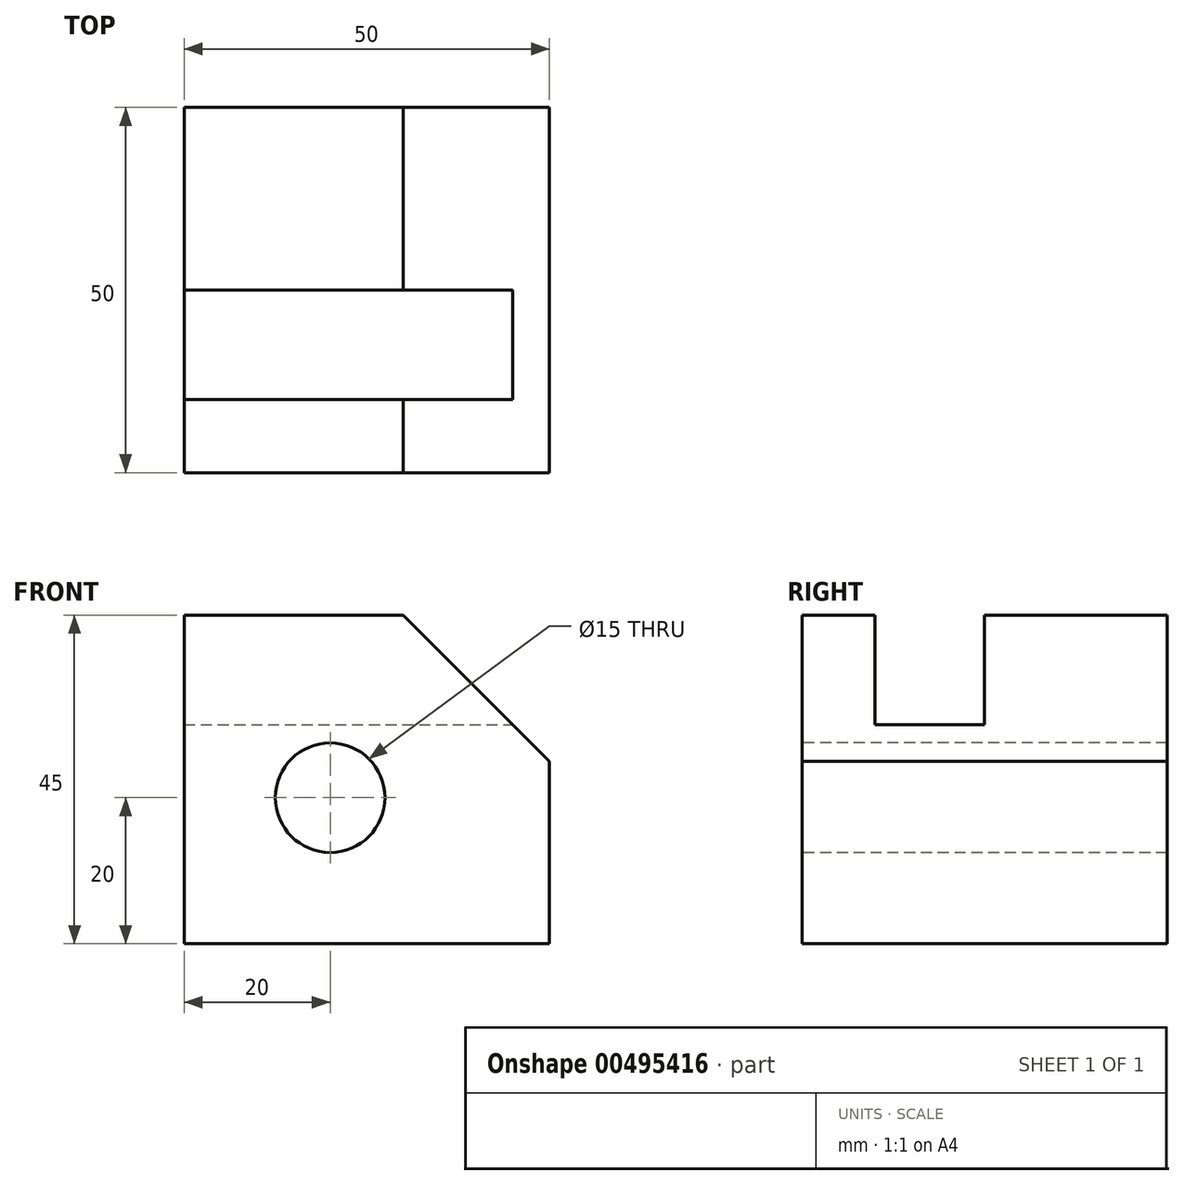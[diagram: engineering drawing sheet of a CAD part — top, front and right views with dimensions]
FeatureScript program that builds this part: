
annotation { "Feature Type Name" : "Feature", "Feature Type Description" : "" }
export const myFeature = defineFeature(function(context is Context, id is Id, definition is map)
    precondition{}
    {
        {
            var Q0;
            Q0=qCreatedBy(makeId("Front.planeOp"),FACE);
            var sketch = newSketch(context, id + "F0", { "sketchPlane" : qUnion([Q0])});
            skLineSegment(sketch, "E0", {"start": v(0, 0) * mm, "end": v(0, 45) * mm});
            skLineSegment(sketch, "E1", {"start": v(0, 45) * mm, "end": v(30, 45) * mm});
            skLineSegment(sketch, "E2", {"start": v(30, 45) * mm, "end": v(50, 25) * mm});
            skLineSegment(sketch, "E3", {"start": v(50, 25) * mm, "end": v(50, 0) * mm});
            skLineSegment(sketch, "E4", {"start": v(50, 0) * mm, "end": v(0, 0) * mm});
            skSolve(sketch);
        }
        {
            var Q0;
            Q0 = qSketchRegion(id + "F0", true);
            extrude(context, id + "F1", {"entities" : qUnion([Q0]), "depth" : 50 * mm});
        }
        {
            var Q0;
            Q0=makeQuery(id+"F1.opExtrude","CAP_FACE",FACE,{"disambiguationData":[OSD([sQuery(id+"F0.wireOp",EDGE,"E0"),sQuery(id+"F0.wireOp",EDGE,"E1"),sQuery(id+"F0.wireOp",EDGE,"E2"),sQuery(id+"F0.wireOp",EDGE,"E3"),sQuery(id+"F0.wireOp",EDGE,"E4")])],"isStart":false});
            var sketch = newSketch(context, id + "F2", { "sketchPlane" : qUnion([Q0])});
            skCircle(sketch, "E5", {"center": v(20, 20) * mm, "radius": 7.5 * mm});
            skSolve(sketch);
        }
        {
            var Q0;
            Q0 = qSketchRegion(id + "F2", true);
            extrude(context, id + "F3", {"entities" : qUnion([Q0]), "operationType" : NewBodyOperationType.REMOVE, "endBound" : BoundingType.THROUGH_ALL, "oppositeDirection" : true, "depth" : 25 * mm});
        }
        {
            var Q0;
            Q0=makeQuery(id+"F1.opExtrude","SWEPT_FACE",FACE,{"disambiguationData":[OSD([sQuery(id+"F0.wireOp",EDGE,"E4")])]});
            cPlane(context, id + "F4", {"entities" : qUnion([Q0]), "cplaneType" : CPlaneType.OFFSET, "offset" : 30 * mm, "oppositeDirection" : true, "width" : 150 * mm, "height" : 150 * mm});
        }
        {
            var Q0;
            Q0=makeQuery(id+"F1.opExtrude","SWEPT_FACE",FACE,{"disambiguationData":[OSD([sQuery(id+"F0.wireOp",EDGE,"E1")])]});
            var sketch = newSketch(context, id + "F5", { "sketchPlane" : qUnion([Q0])});
            skLineSegment(sketch, "E6.bottom", {"start": v(0, -40) * mm, "end": v(50, -40) * mm});
            skLineSegment(sketch, "E6.top", {"start": v(0, -25) * mm, "end": v(50, -25) * mm});
            skLineSegment(sketch, "E6.left", {"start": v(0, -40) * mm, "end": v(0, -25) * mm});
            skLineSegment(sketch, "E6.right", {"start": v(50, -40) * mm, "end": v(50, -25) * mm});
            skSolve(sketch);
        }
        {
            var Q0;
            Q0 = qSketchRegion(id + "F5", true);
            var Q1;
            Q1=qCreatedBy(id+"F4.planeOp",FACE);
            extrude(context, id + "F6", {"entities" : qUnion([Q0]), "operationType" : NewBodyOperationType.REMOVE, "endBound" : BoundingType.UP_TO_SURFACE, "oppositeDirection" : true, "endBoundEntityFace" : qUnion([Q1]), "depth" : 25 * mm});
        }
    });
